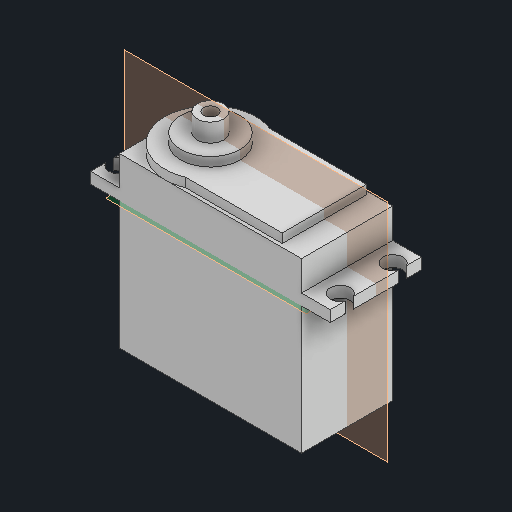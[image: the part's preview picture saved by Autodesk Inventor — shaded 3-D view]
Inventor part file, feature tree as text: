
AUTODESK INVENTOR PART (.ipt)
format: ipt  version: 2024 (Build 280153000, 153)  size: 259,584 bytes
history: native  units: in
note: dims shown in document units (in); Inventor stores cm internally (conversion verified against a paired STEP export)
features: projected_geometry x6, extrude x5, sketch x5, plane x1
ambient origin geometry x8: Origin, YZ Plane, XZ Plane, XY Plane, X Axis, Y Axis, Z Axis, Center Point
bodies: Solid1 (feature_tree)
feature tree (17):
  extrude  "Extrusion1"  Depth=0.7874in
  extrude  "Extrusion2"  Depth=0.1969in
  extrude  "Extrusion3"  Depth=0.0787in TaperAngle=0.0deg
  extrude  "Extrusion4"  Depth=0.0787in TaperAngle=0.0deg
  plane  "Work Plane1"
  extrude  "Extrusion5"  Depth=0.0965in
  sketch  "Sketch1"  dims[d0=1.5748in d1=0.7874in]
  sketch  "Sketch2"  dims[d2=1.4567in d3=0.0in d4=0.1969in]
  projected_geometry  "Projected Loop1"
  sketch  "Sketch3"  dims[d5=0.0295in d6=0.0787in d7=0.0in]
  projected_geometry  "Projected Loop2"
  sketch  "Sketch4"  dims[d8=0.5118in d9=0.0787in d10=0.0in]
  projected_geometry  "Projected Loop3"
  sketch  "Sketch5"  dims[d11=0.2283in d12=0.1181in d13=0.1575in d14=0.0in d15=-1.1024in d16=0.248in d17=0.248in d18=0.1732in d19=0.0827in d20=0.0787in d21=0.0965in d22=0.0in]
  projected_geometry  "Projected Loop4"
  projected_geometry  "Projected Loop5"
  projected_geometry  "Projected Loop6"
